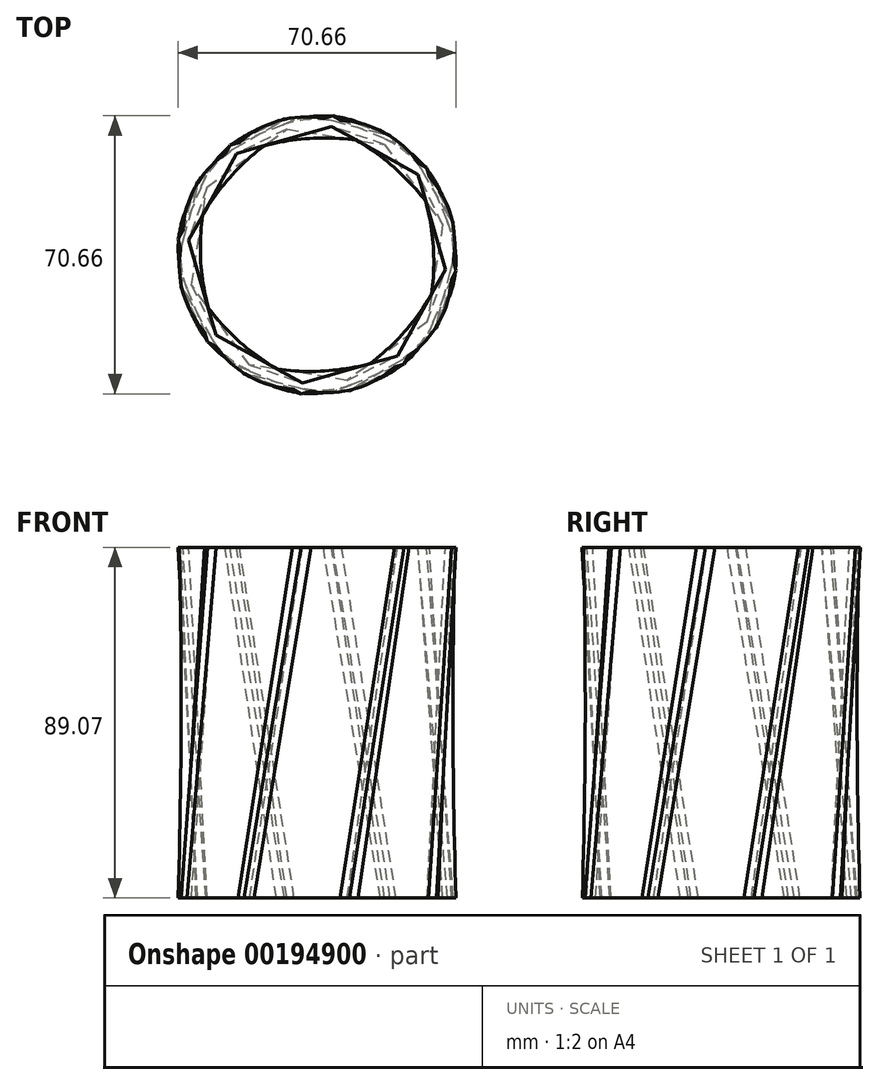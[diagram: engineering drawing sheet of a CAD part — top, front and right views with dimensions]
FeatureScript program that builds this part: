
annotation { "Feature Type Name" : "Feature", "Feature Type Description" : "" }
export const myFeature = defineFeature(function(context is Context, id is Id, definition is map)
    precondition{}
    {
        {
            var Q0;
            Q0=qCreatedBy(makeId("Top.planeOp"),FACE);
            var sketch = newSketch(context, id + "F0", { "sketchPlane" : qUnion([Q0])});
            skLineSegment(sketch, "E0", {"start": v(8.3, -34.58) * mm, "end": v(10.36, -33.08) * mm});
            skLineSegment(sketch, "E1", {"start": v(28.27, -20.07) * mm, "end": v(30.32, -18.58) * mm});
            skArc(sketch, "E2", {"start": v(10.36, -33.08) * mm, "mid": v(20.8, -28.63) * mm, "end": v(28.27, -20.07) * mm});
            skLineSegment(sketch, "E3", {"start": v(10.36, -33.08) * mm, "end": v(28.27, -20.07) * mm, "construction": true});
            skLineSegment(sketch, "E4", {"start": v(8.3, -34.58) * mm, "end": v(0, 0) * mm, "construction": true});
            skLineSegment(sketch, "E5", {"start": v(0, 0) * mm, "end": v(30.32, -18.58) * mm, "construction": true});
            skPoint(sketch, "E6", {"position": v(20.8, -28.63) * mm});
            skLineSegment(sketch, "E7", {"start": v(30.32, -18.58) * mm, "end": v(27.98, -17.14) * mm});
            skLineSegment(sketch, "E8", {"start": v(8.3, -34.58) * mm, "end": v(7.66, -31.9) * mm});
            skLineSegment(sketch, "E9", {"start": v(27.98, -17.14) * mm, "end": v(7.66, -31.9) * mm});
            skSolve(sketch);
        }
        {
            var Q0;
            Q0=qCreatedBy(makeId("Front.planeOp"),FACE);
            var sketch = newSketch(context, id + "F1", { "sketchPlane" : qUnion([Q0])});
            skLineSegment(sketch, "E10", {"start": v(0, 0) * mm, "end": v(0, 89.07) * mm});
            skSolve(sketch);
        }
        {
            var Q0;
            Q0=qCreatedBy(makeId("Top.planeOp"),FACE);
            var Q1;
            Q1=sQuery(id+"F1.wireOp",VERTEX,"E10.end");
            cPlane(context, id + "F2", {"entities" : qUnion([Q0, Q1]), "cplaneType" : CPlaneType.PLANE_POINT, "offset" : 25.4 * mm, "width" : 152.4 * mm, "height" : 152.4 * mm});
        }
        {
            var Q0;
            Q0=qCreatedBy(id+"F2.planeOp",FACE);
            var sketch = newSketch(context, id + "F3", { "sketchPlane" : qUnion([Q0])});
            skLineSegment(sketch, "E11.0", {"start": v(32.6, -3.71) * mm, "end": v(20.43, -25.68) * mm});
            skLineSegment(sketch, "E12.0", {"start": v(22.14, -27.83) * mm, "end": v(20.43, -25.68) * mm});
            skLineSegment(sketch, "E13.0", {"start": v(22.14, -27.83) * mm, "end": v(23.37, -25.6) * mm});
            skArc(sketch, "E14.0", {"start": v(23.37, -25.6) * mm, "mid": v(30.96, -17.16) * mm, "end": v(34.1, -6.25) * mm});
            skLineSegment(sketch, "E15.0", {"start": v(34.1, -6.25) * mm, "end": v(35.33, -4.03) * mm});
            skLineSegment(sketch, "E16.0", {"start": v(35.33, -4.03) * mm, "end": v(32.6, -3.71) * mm});
            skSolve(sketch);
        }
        {
            var Q0;
            Q0=qSketchRegion(id+"F0",true);
            var Q1;
            Q1=qSketchRegion(id+"F3",true);
            var Q2;
            Q2=qConstructionFilter(qBodyType(qCreatedBy(id+"F0",EDGE),BodyType.WIRE),ConstructionObject.NO);
            var Q3;
            Q3=qConstructionFilter(qBodyType(qCreatedBy(id+"F3",EDGE),BodyType.WIRE),ConstructionObject.NO);
            loft(context, id + "F4", {"sheetProfilesArray" : [{ "sheetProfileEntities" : qUnion([Q0]) }, { "sheetProfileEntities" : qUnion([Q1]) }], "wireProfilesArray" : [{ "wireProfileEntities" : qUnion([Q2]) }, { "wireProfileEntities" : qUnion([Q3]) }]});
        }
        {
            var Q0;
            Q0=makeQuery(id+"F4.opLoft","SWEPT_BODY",BODY,{"disambiguationData":[OSD([makeQuery(id+"F0.imprint","IMPRINT",FACE,{"disambiguationData":[TD([[makeQuery(id+"F0.imprint","IMPRINT",EDGE,{"derivedFrom":sQuery(id+"F0.wireOp",EDGE,"E0")}),1.0]])]}),makeQuery(id+"F3.imprint","IMPRINT",FACE,{"disambiguationData":[TD([[makeQuery(id+"F3.imprint","IMPRINT",EDGE,{"derivedFrom":sQuery(id+"F3.wireOp",EDGE,"E11.0")}),1.0]])]})])]});
            var Q1;
            Q1=sQuery(id+"F1.wireOp",EDGE,"E10");
            circularPattern(context, id + "F5", {"operationType" : NewBodyOperationType.ADD, "entities" : qUnion([Q0]), "axis" : qUnion([Q1]), "angle" : 45 * degree, "instanceCount" : 8, "computeTransformsWithoutBuiltin" : true});
        }
    });
